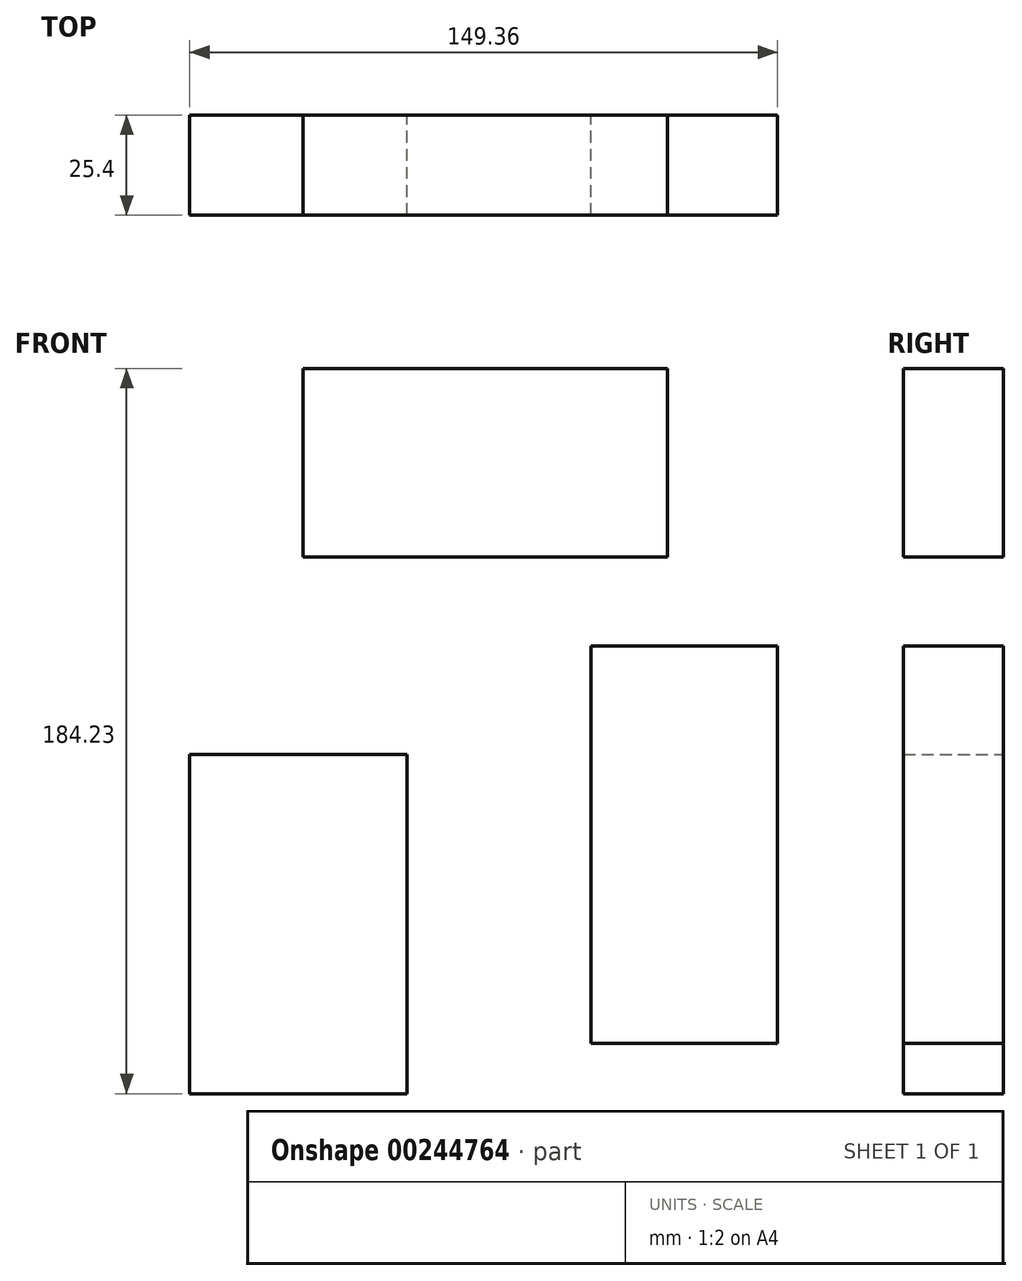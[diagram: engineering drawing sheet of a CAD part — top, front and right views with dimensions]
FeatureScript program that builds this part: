
annotation { "Feature Type Name" : "Feature", "Feature Type Description" : "" }
export const myFeature = defineFeature(function(context is Context, id is Id, definition is map)
    precondition{}
    {
        {
            var Q0;
            Q0=qCreatedBy(makeId("Front.planeOp"),FACE);
            var sketch = newSketch(context, id + "F1", { "sketchPlane" : qUnion([Q0])});
            skLineSegment(sketch, "E0.bottom", {"start": v(-33.02, 119.33) * mm, "end": v(59.6, 119.33) * mm});
            skLineSegment(sketch, "E0.top", {"start": v(-33.02, 71.4) * mm, "end": v(59.6, 71.4) * mm});
            skLineSegment(sketch, "E0.left", {"start": v(-33.02, 119.33) * mm, "end": v(-33.02, 71.4) * mm});
            skLineSegment(sketch, "E0.right", {"start": v(59.6, 119.33) * mm, "end": v(59.6, 71.4) * mm});
            skLineSegment(sketch, "E1.bottom", {"start": v(-61.8, 21.27) * mm, "end": v(-6.6, 21.27) * mm});
            skLineSegment(sketch, "E1.top", {"start": v(-61.8, -64.9) * mm, "end": v(-6.6, -64.9) * mm});
            skLineSegment(sketch, "E1.left", {"start": v(-61.8, 21.27) * mm, "end": v(-61.8, -64.9) * mm});
            skLineSegment(sketch, "E1.right", {"start": v(-6.6, 21.27) * mm, "end": v(-6.6, -64.9) * mm});
            skLineSegment(sketch, "E2.bottom", {"start": v(40.13, 48.84) * mm, "end": v(87.55, 48.84) * mm});
            skLineSegment(sketch, "E2.top", {"start": v(40.13, -52.11) * mm, "end": v(87.55, -52.11) * mm});
            skLineSegment(sketch, "E2.left", {"start": v(40.13, 48.84) * mm, "end": v(40.13, -52.11) * mm});
            skLineSegment(sketch, "E2.right", {"start": v(87.55, 48.84) * mm, "end": v(87.55, -52.11) * mm});
            skSolve(sketch);
        }
        {
            var Q0;
            Q0 = qSketchRegion(id + "F1", true);
            extrude(context, id + "F0", {"entities" : qUnion([Q0]), "depth" : 25.4 * mm});
        }
    });
